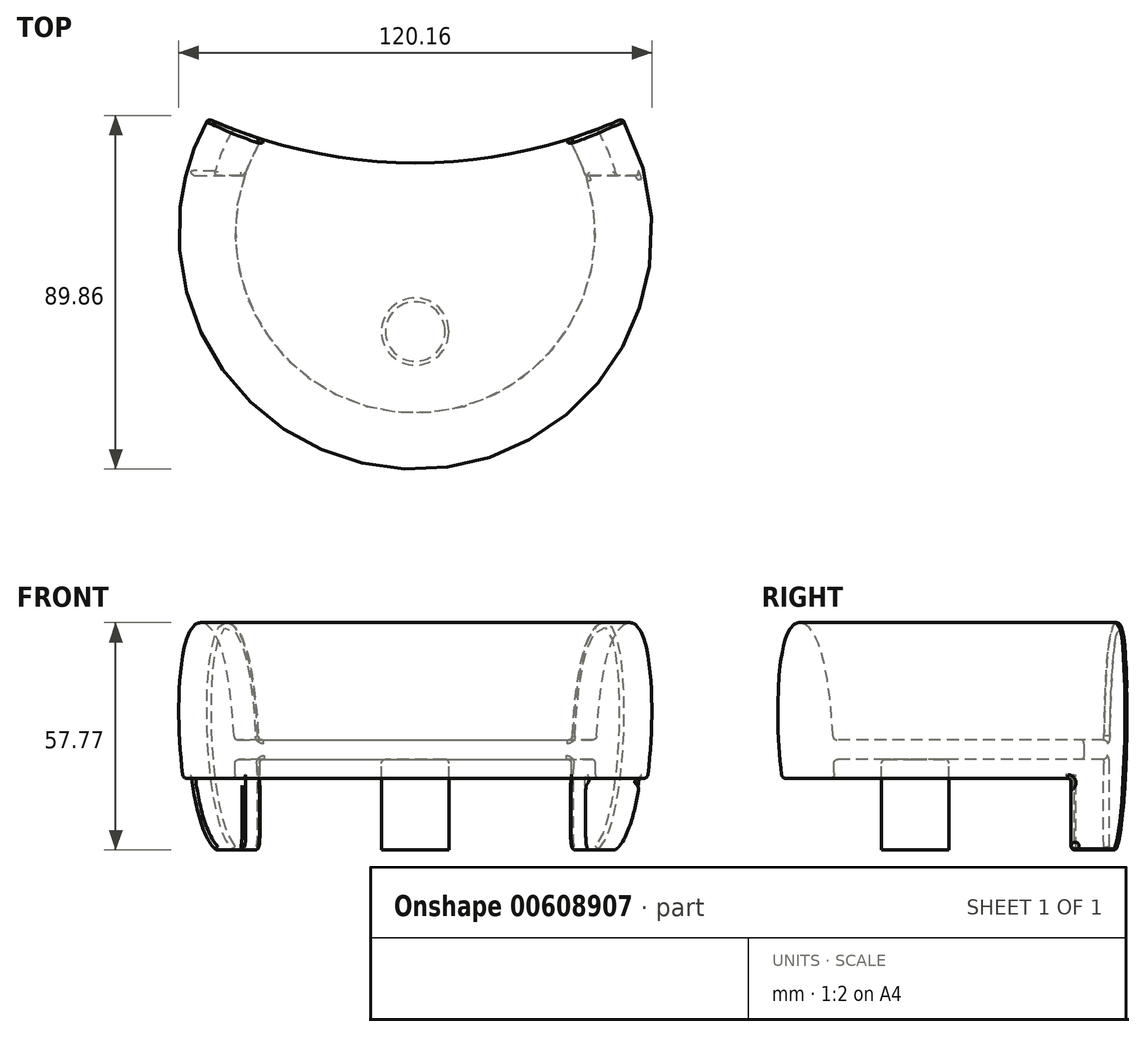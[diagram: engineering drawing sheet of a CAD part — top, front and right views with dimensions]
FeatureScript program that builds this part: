
annotation { "Feature Type Name" : "Feature", "Feature Type Description" : "" }
export const myFeature = defineFeature(function(context is Context, id is Id, definition is map)
    precondition{}
    {
        {
            var Q0;
            Q0=qCreatedBy(makeId("Top.planeOp"),FACE);
            var sketch = newSketch(context, id + "F0", { "sketchPlane" : qUnion([Q0])});
            skCircle(sketch, "E0", {"center": v(0, 0) * mm, "radius": 50 * mm});
            skSolve(sketch);
        }
        {
            var Q0;
            Q0=qCreatedBy(makeId("Front.planeOp"),FACE);
            var sketch = newSketch(context, id + "F1", { "sketchPlane" : qUnion([Q0])});
            skFitSpline(sketch, "E1", {"points": [v(-47.06, -23.78) * mm, v(-54.2, -21.52) * mm, v(-56.84, 33.36) * mm, v(-50.5, 31.1) * mm, v(-45.64, -17.4) * mm, v(-47.06, -23.78) * mm]});
            skSolve(sketch);
        }
        {
            var Q0;
            Q0=makeQuery(id+"F1.imprint","IMPRINT",FACE,{"disambiguationData":[TD([[makeQuery(id+"F1.imprint","IMPRINT",EDGE,{"derivedFrom":sQuery(id+"F1.wireOp",EDGE,"E1")}),-1.0]])]});
            var Q1;
            Q1=sQuery(id+"F1.wireOp",EDGE,"E1");
            var Q2;
            Q2=sQuery(id+"F0.wireOp",EDGE,"E0");
            revolve(context, id + "F2", {"entities" : qUnion([Q0]), "surfaceEntities" : qUnion([Q1]), "axis" : qUnion([Q2]), "revolveType" : RevolveType.FULL});
        }
        {
            var Q0;
            Q0=makeQuery(id+"F0.imprint","IMPRINT",FACE,{"disambiguationData":[TD([[makeQuery(id+"F0.imprint","IMPRINT",EDGE,{"derivedFrom":sQuery(id+"F0.wireOp",EDGE,"E0")}),1.0]])]});
            extrude(context, id + "F3", {"entities" : qUnion([Q0]), "operationType" : NewBodyOperationType.ADD, "depth" : 5 * mm, "offsetDistance" : 25 * mm});
        }
        {
            var Q0;
            Q0=qCreatedBy(makeId("Top.planeOp"),FACE);
            cPlane(context, id + "F4", {"entities" : qUnion([Q0]), "cplaneType" : CPlaneType.OFFSET, "offset" : 30 * mm, "oppositeDirection" : true, "width" : 150 * mm, "height" : 150 * mm});
        }
        {
            var Q0;
            Q0=qCreatedBy(id+"F4.planeOp",FACE);
            var sketch = newSketch(context, id + "F5", { "sketchPlane" : qUnion([Q0])});
            skCircle(sketch, "E2", {"center": v(0, 146.8) * mm, "radius": 129.05 * mm});
            skSolve(sketch);
        }
        {
            var Q0;
            Q0=makeQuery(id+"F5.imprint","IMPRINT",FACE,{"disambiguationData":[TD([[makeQuery(id+"F5.imprint","IMPRINT",EDGE,{"derivedFrom":sQuery(id+"F5.wireOp",EDGE,"E2")}),1.0]])]});
            extrude(context, id + "F6", {"entities" : qUnion([Q0]), "operationType" : NewBodyOperationType.REMOVE, "depth" : 91 * mm, "offsetDistance" : 25 * mm});
        }
        {
            var Q0;
            Q0=qCreatedBy(makeId("Right.planeOp"),FACE);
            cPlane(context, id + "F7", {"entities" : qUnion([Q0]), "cplaneType" : CPlaneType.OFFSET, "offset" : 100 * mm, "width" : 150 * mm, "height" : 150 * mm});
        }
        {
            var Q0;
            Q0=qCreatedBy(id+"F7.planeOp",FACE);
            var sketch = newSketch(context, id + "F8", { "sketchPlane" : qUnion([Q0])});
            skLineSegment(sketch, "E3.bottom", {"start": v(14.45, -4.8) * mm, "end": v(-68.24, -4.8) * mm});
            skLineSegment(sketch, "E3.top", {"start": v(14.45, -31.86) * mm, "end": v(-68.24, -31.86) * mm});
            skLineSegment(sketch, "E3.left", {"start": v(14.45, -4.8) * mm, "end": v(14.45, -31.86) * mm});
            skLineSegment(sketch, "E3.right", {"start": v(-68.24, -4.8) * mm, "end": v(-68.24, -31.86) * mm});
            skSolve(sketch);
        }
        {
            var Q0;
            Q0=makeQuery(id+"F8.imprint","IMPRINT",FACE,{"disambiguationData":[TD([[makeQuery(id+"F8.imprint","IMPRINT",EDGE,{"derivedFrom":sQuery(id+"F8.wireOp",EDGE,"E3.bottom")}),1.0]])]});
            extrude(context, id + "F9", {"entities" : qUnion([Q0]), "operationType" : NewBodyOperationType.REMOVE, "oppositeDirection" : true, "depth" : 188.9 * mm, "offsetDistance" : 25 * mm});
        }
        {
            var Q0;
            Q0=qCreatedBy(makeId("Top.planeOp"),FACE);
            var sketch = newSketch(context, id + "F10", { "sketchPlane" : qUnion([Q0])});
            skCircle(sketch, "E4", {"center": v(0, -25.12) * mm, "radius": 8.56 * mm});
            skSolve(sketch);
        }
        {
            var Q0;
            Q0=makeQuery(id+"F10.imprint","IMPRINT",FACE,{"disambiguationData":[TD([[makeQuery(id+"F10.imprint","IMPRINT",EDGE,{"derivedFrom":sQuery(id+"F10.wireOp",EDGE,"E4")}),1.0]])]});
            var Q1;
            Q1 = qConstructionFilter(qBodyType(qCreatedBy(id + "F10" ,EDGE), BodyType.WIRE), ConstructionObject.NO);
            extrude(context, id + "F11", {"entities" : qUnion([Q0]), "surfaceEntities" : qUnion([Q1]), "oppositeDirection" : true, "depth" : 52.73 * mm, "offsetDistance" : 25 * mm});
        }
        {
            var Q0;
            Q0=qCreatedBy(id+"F7.planeOp",FACE);
            var sketch = newSketch(context, id + "F12", { "sketchPlane" : qUnion([Q0])});
            skLineSegment(sketch, "E5.bottom", {"start": v(32.68, -23.02) * mm, "end": v(-67.12, -23.02) * mm});
            skLineSegment(sketch, "E5.top", {"start": v(32.68, -59.86) * mm, "end": v(-67.12, -59.86) * mm});
            skLineSegment(sketch, "E5.left", {"start": v(32.68, -23.02) * mm, "end": v(32.68, -59.86) * mm});
            skLineSegment(sketch, "E5.right", {"start": v(-67.12, -23.02) * mm, "end": v(-67.12, -59.86) * mm});
            skSolve(sketch);
        }
        {
            var Q0;
            Q0=makeQuery(id+"F12.imprint","IMPRINT",FACE,{"disambiguationData":[TD([[makeQuery(id+"F12.imprint","IMPRINT",EDGE,{"derivedFrom":sQuery(id+"F12.wireOp",EDGE,"E5.bottom")}),1.0]])]});
            extrude(context, id + "F13", {"entities" : qUnion([Q0]), "operationType" : NewBodyOperationType.REMOVE, "oppositeDirection" : true, "depth" : 200 * mm, "offsetDistance" : 25 * mm});
        }
        {
            var Q0;
            Q0=makeQuery(id+"F12.imprint","IMPRINT",FACE,{"disambiguationData":[TD([[makeQuery(id+"F12.imprint","IMPRINT",EDGE,{"derivedFrom":sQuery(id+"F12.wireOp",EDGE,"E5.bottom")}),1.0]])]});
            extrude(context, id + "F14", {"entities" : qUnion([Q0]), "operationType" : NewBodyOperationType.REMOVE, "oppositeDirection" : true, "depth" : 208.9 * mm, "offsetDistance" : 25 * mm});
        }
        {
            var Q0;
            Q0=makeQuery(id+"F6.boolean.opBoolean","INTERSECT",EDGE,{"derivedFrom":[makeQuery(id+"F3.opExtrude","CAP_FACE",FACE,{"disambiguationData":[OSD([sQuery(id+"F0.wireOp",EDGE,"E0")])],"isStart":false}),makeQuery(id+"F6.opExtrude","SWEPT_FACE",FACE,{"disambiguationData":[OSD([sQuery(id+"F5.wireOp",EDGE,"E2")])]})]});
            var Q1;
            Q1=makeQuery(id+"F13.boolean.opBoolean","INTERSECT",EDGE,{"disambiguationData":[OD(1.0)],"derivedFrom":[makeQuery(id+"F6.boolean.opBoolean","COPY",FACE,{"derivedFrom":makeQuery(id+"F6.opExtrude","SWEPT_FACE",FACE,{"disambiguationData":[OSD([sQuery(id+"F5.wireOp",EDGE,"E2")])]})}),makeQuery(id+"F13.opExtrude","SWEPT_FACE",FACE,{"disambiguationData":[OSD([sQuery(id+"F12.wireOp",EDGE,"E5.bottom")])]})]});
            var Q2;
            Q2=makeQuery(id+"F6.boolean.opBoolean","COPY",FACE,{"derivedFrom":makeQuery(id+"F6.opExtrude","SWEPT_FACE",FACE,{"disambiguationData":[OSD([sQuery(id+"F5.wireOp",EDGE,"E2")])]})});
            var Q3;
            Q3=makeQuery(id+"F9.boolean.opBoolean","INTERSECT",EDGE,{"disambiguationData":[OD(1.0)],"derivedFrom":[makeQuery(id+"F2.opRevolve","SWEPT_FACE",FACE,{"disambiguationData":[OSD([sQuery(id+"F1.wireOp",EDGE,"E1")])]}),makeQuery(id+"F9.opExtrude","SWEPT_FACE",FACE,{"disambiguationData":[OSD([sQuery(id+"F8.wireOp",EDGE,"E3.bottom")])]})]});
            var Q4;
            Q4=makeQuery(id+"F3.boolean.opBoolean","INTERSECT",EDGE,{"derivedFrom":[makeQuery(id+"F2.opRevolve","SWEPT_FACE",FACE,{"disambiguationData":[OSD([sQuery(id+"F1.wireOp",EDGE,"E1")])]}),makeQuery(id+"F3.opExtrude","CAP_FACE",FACE,{"disambiguationData":[OSD([sQuery(id+"F0.wireOp",EDGE,"E0")])],"isStart":true})]});
            var Q5;
            Q5=makeQuery(id+"F13.boolean.opBoolean","INTERSECT",EDGE,{"derivedFrom":[makeQuery(id+"F9.boolean.opBoolean","COPY",FACE,{"disambiguationData":[OD(1.0)],"derivedFrom":makeQuery(id+"F9.opExtrude","SWEPT_FACE",FACE,{"disambiguationData":[OSD([sQuery(id+"F8.wireOp",EDGE,"E3.left")])]})}),makeQuery(id+"F13.opExtrude","SWEPT_FACE",FACE,{"disambiguationData":[OSD([sQuery(id+"F12.wireOp",EDGE,"E5.bottom")])]})]});
            var Q6;
            Q6=makeQuery(id+"F13.boolean.opBoolean","INTERSECT",EDGE,{"disambiguationData":[OD(1.0)],"derivedFrom":[makeQuery(id+"F2.opRevolve","SWEPT_FACE",FACE,{"disambiguationData":[OSD([sQuery(id+"F1.wireOp",EDGE,"E1")])]}),makeQuery(id+"F13.opExtrude","SWEPT_FACE",FACE,{"disambiguationData":[OSD([sQuery(id+"F12.wireOp",EDGE,"E5.bottom")])]})]});
            var Q7;
            Q7=makeQuery(id+"F9.boolean.opBoolean","COPY",EDGE,{"disambiguationData":[OD(1.0)],"derivedFrom":makeQuery(id+"F9.opExtrude","SWEPT_EDGE",EDGE,{"disambiguationData":[OSD([sQuery(id+"F8.wireOp",EDGE,"E3.bottom"),sQuery(id+"F8.wireOp",EDGE,"E3.left")])]})});
            var Q8;
            Q8=makeQuery(id+"F9.boolean.opBoolean","INTERSECT",EDGE,{"disambiguationData":[OD(0.0)],"derivedFrom":[makeQuery(id+"F2.opRevolve","SWEPT_FACE",FACE,{"disambiguationData":[OSD([sQuery(id+"F1.wireOp",EDGE,"E1")])]}),makeQuery(id+"F9.opExtrude","SWEPT_FACE",FACE,{"disambiguationData":[OSD([sQuery(id+"F8.wireOp",EDGE,"E3.bottom")])]})]});
            var Q9;
            Q9=makeQuery(id+"F13.boolean.opBoolean","INTERSECT",EDGE,{"disambiguationData":[OD(2.0)],"derivedFrom":[makeQuery(id+"F2.opRevolve","SWEPT_FACE",FACE,{"disambiguationData":[OSD([sQuery(id+"F1.wireOp",EDGE,"E1")])]}),makeQuery(id+"F13.opExtrude","SWEPT_FACE",FACE,{"disambiguationData":[OSD([sQuery(id+"F12.wireOp",EDGE,"E5.bottom")])]})]});
            var Q10;
            Q10=makeQuery(id+"F13.boolean.opBoolean","INTERSECT",EDGE,{"disambiguationData":[OD(3.0)],"derivedFrom":[makeQuery(id+"F2.opRevolve","SWEPT_FACE",FACE,{"disambiguationData":[OSD([sQuery(id+"F1.wireOp",EDGE,"E1")])]}),makeQuery(id+"F13.opExtrude","SWEPT_FACE",FACE,{"disambiguationData":[OSD([sQuery(id+"F12.wireOp",EDGE,"E5.bottom")])]})]});
            var Q11;
            Q11=makeQuery(id+"F13.boolean.opBoolean","SPLIT",EDGE,{"disambiguationData":[OD(1.0)],"derivedFrom":makeQuery(id+"F9.boolean.opBoolean","INTERSECT",EDGE,{"disambiguationData":[OD(0.0)],"derivedFrom":[makeQuery(id+"F2.opRevolve","SWEPT_FACE",FACE,{"disambiguationData":[OSD([sQuery(id+"F1.wireOp",EDGE,"E1")])]}),makeQuery(id+"F9.opExtrude","SWEPT_FACE",FACE,{"disambiguationData":[OSD([sQuery(id+"F8.wireOp",EDGE,"E3.left")])]})]})});
            var Q12;
            Q12=makeQuery(id+"F13.boolean.opBoolean","INTERSECT",EDGE,{"disambiguationData":[OD(0.0)],"derivedFrom":[makeQuery(id+"F2.opRevolve","SWEPT_FACE",FACE,{"disambiguationData":[OSD([sQuery(id+"F1.wireOp",EDGE,"E1")])]}),makeQuery(id+"F13.opExtrude","SWEPT_FACE",FACE,{"disambiguationData":[OSD([sQuery(id+"F12.wireOp",EDGE,"E5.bottom")])]})]});
            var Q13;
            Q13=makeQuery(id+"F13.boolean.opBoolean","INTERSECT",EDGE,{"derivedFrom":[makeQuery(id+"F9.boolean.opBoolean","COPY",FACE,{"disambiguationData":[OD(0.0)],"derivedFrom":makeQuery(id+"F9.opExtrude","SWEPT_FACE",FACE,{"disambiguationData":[OSD([sQuery(id+"F8.wireOp",EDGE,"E3.left")])]})}),makeQuery(id+"F13.opExtrude","SWEPT_FACE",FACE,{"disambiguationData":[OSD([sQuery(id+"F12.wireOp",EDGE,"E5.bottom")])]})]});
            var Q14;
            Q14=makeQuery(id+"F13.boolean.opBoolean","SPLIT",EDGE,{"disambiguationData":[OD(0.0)],"derivedFrom":makeQuery(id+"F9.boolean.opBoolean","INTERSECT",EDGE,{"disambiguationData":[OD(0.0)],"derivedFrom":[makeQuery(id+"F2.opRevolve","SWEPT_FACE",FACE,{"disambiguationData":[OSD([sQuery(id+"F1.wireOp",EDGE,"E1")])]}),makeQuery(id+"F9.opExtrude","SWEPT_FACE",FACE,{"disambiguationData":[OSD([sQuery(id+"F8.wireOp",EDGE,"E3.left")])]})]})});
            var Q15;
            Q15=makeQuery(id+"F14.boolean.opBoolean","INTERSECT",EDGE,{"derivedFrom":[makeQuery(id+"F11.opExtrude","SWEPT_FACE",FACE,{"disambiguationData":[OSD([sQuery(id+"F10.wireOp",EDGE,"E4")])]}),makeQuery(id+"F14.opExtrude","SWEPT_FACE",FACE,{"disambiguationData":[OSD([sQuery(id+"F12.wireOp",EDGE,"E5.bottom")])]})]});
            var Q16;
            Q16=makeQuery(id+"F11.opExtrude","CAP_EDGE",EDGE,{"disambiguationData":[OSD([sQuery(id+"F10.wireOp",EDGE,"E4")])],"isStart":true});
            var Q17;
            Q17=makeQuery(id+"F3.boolean.opBoolean","INTERSECT",EDGE,{"derivedFrom":[makeQuery(id+"F2.opRevolve","SWEPT_FACE",FACE,{"disambiguationData":[OSD([sQuery(id+"F1.wireOp",EDGE,"E1")])]}),makeQuery(id+"F3.opExtrude","CAP_FACE",FACE,{"disambiguationData":[OSD([sQuery(id+"F0.wireOp",EDGE,"E0")])],"isStart":false})]});
            fillet(context, id + "F15", {"entities" : qUnion([Q0, Q1, Q2, Q3, Q4, Q5, Q6, Q7, Q8, Q9, Q10, Q11, Q12, Q13, Q14, Q15, Q16, Q17]), "radius" : 1 * mm, "tangentPropagation" : true, "allowEdgeOverflow" : false});
        }
    });
